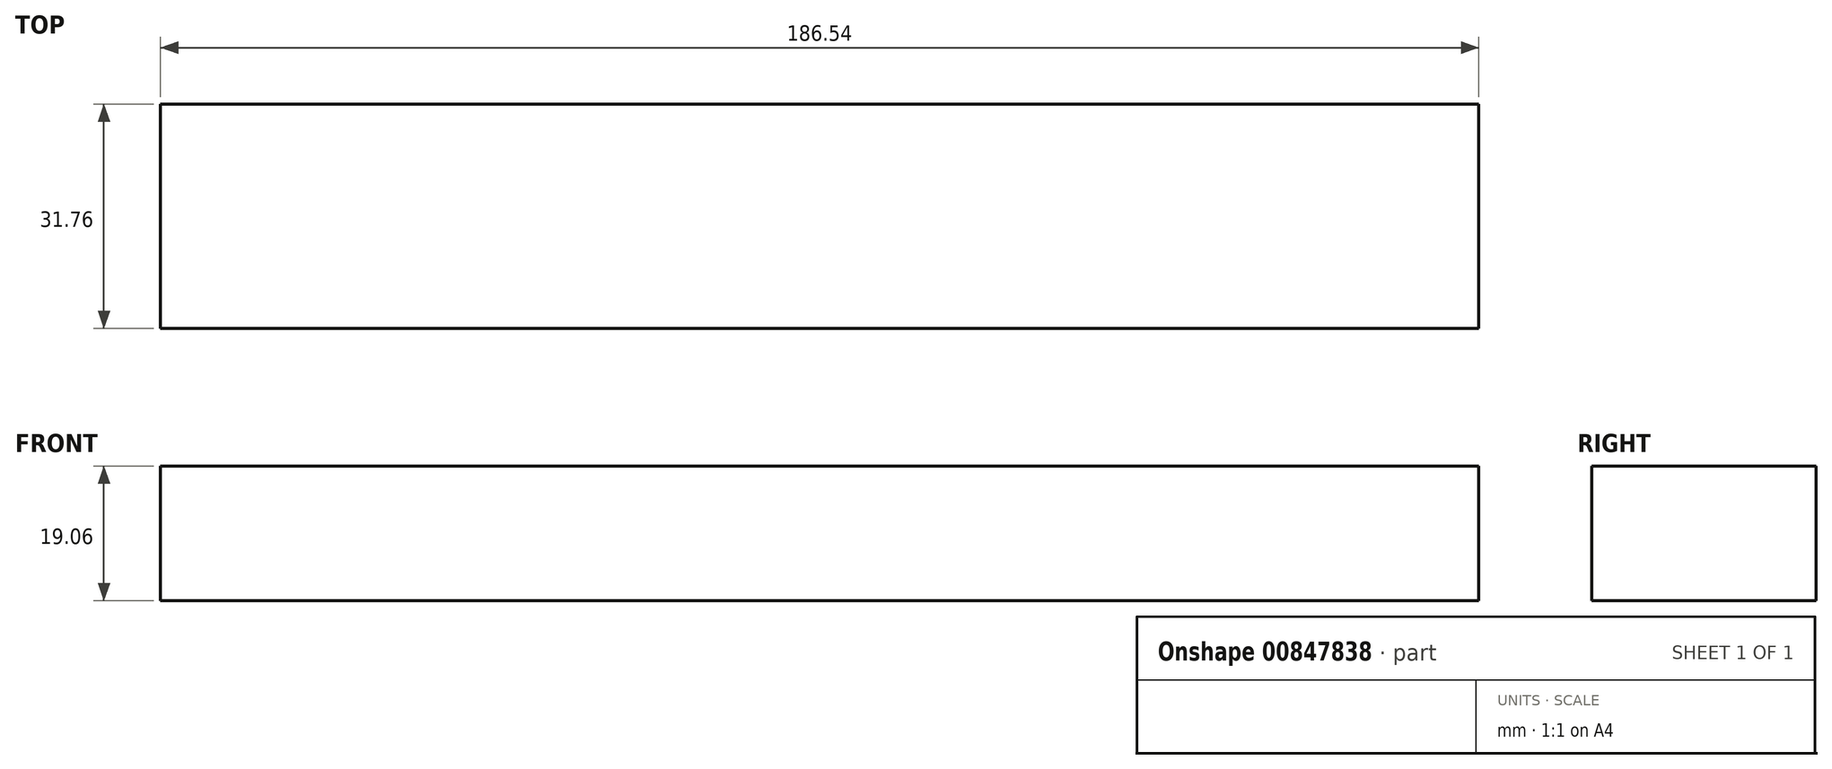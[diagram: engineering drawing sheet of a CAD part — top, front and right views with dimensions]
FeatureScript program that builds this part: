
annotation { "Feature Type Name" : "Feature", "Feature Type Description" : "" }
export const myFeature = defineFeature(function(context is Context, id is Id, definition is map)
    precondition{}
    {
        {
            var Q0;
            Q0=qCreatedBy(makeId("Top.planeOp"),FACE);
            var sketch = newSketch(context, id + "F0", { "sketchPlane" : qUnion([Q0])});
            skLineSegment(sketch, "E0.bottom", {"start": v(93.27, -15.87) * mm, "end": v(-93.27, -15.88) * mm});
            skLineSegment(sketch, "E0.top", {"start": v(93.27, 15.88) * mm, "end": v(-93.27, 15.88) * mm});
            skLineSegment(sketch, "E0.left", {"start": v(93.27, -15.87) * mm, "end": v(93.27, 15.88) * mm});
            skLineSegment(sketch, "E0.right", {"start": v(-93.27, -15.88) * mm, "end": v(-93.27, 15.88) * mm});
            skPoint(sketch, "E0.middle", {"position": v(0, 0) * mm});
            skSolve(sketch);
        }
        {
            var Q0;
            Q0 = qSketchRegion(id + "F0", true);
            extrude(context, id + "F1", {"entities" : qUnion([Q0]), "endBound" : BoundingType.SYMMETRIC, "depth" : 19.05 * mm, "offsetDistance" : 25.4 * mm});
        }
    });
